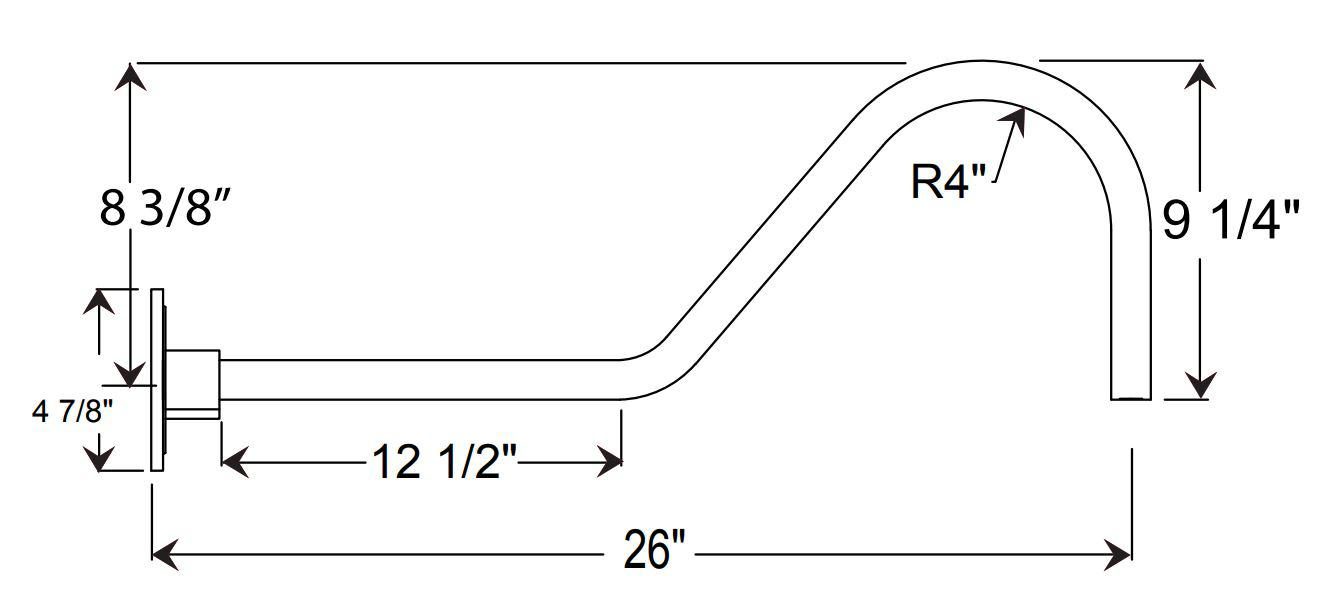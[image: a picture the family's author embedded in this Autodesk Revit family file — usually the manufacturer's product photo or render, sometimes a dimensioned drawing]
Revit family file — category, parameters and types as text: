
# Revit family: OSND MB 24,36,42
name_source: partatom
category: Lighting Fixtures
units: mm (PartAtom-declared; Revit-internal decimal feet)

## family parameters
Always vertical = Yes
Cut with Voids When Loaded = No
Light Source = Yes
OmniClass Number = 23.80.70.00
OmniClass Title = Lighting
Part Type = Normal
Room Calculation Point = No
Round Connector Dimension = Use Diameter
Shared = No
Work Plane-Based = No

## types (3) — shared parameters
Apparent Load = 200 VA
Body Colour = Spun aluminium
Body Material = body
Bulb = Bulb
CRI = >90
Canopy Body = body
Color Filter = 16777215
Construction Material = Heavy Duty spun aluminum.
Default Elevation = 0' - 0"
Description = 120-277 Voltage
Dimming = 1%
Dimming Lamp Color Temperature Shift = <None>
Efficiency = 65-125 lumens per watt
Lamp = MB
Life = L70 50,000 hours
Load Classification = Lighting
Manufacturer = ANP Lighting
Photometric Web File = generic
Power Factor = 1
Tilt Angle = 90.00°
URL = https://www.anplighting.com
Voltage = 277 V
Warranty = 5 year limited warranty
Wattage Comments = 200 W Max

## per-type parameters (varying)
| type | Fixture Diameter | Fixture Height | OSND24 | OSND36 | OSND42 | Weight | a | b |
| OSND24 | 2' - 0" | 1' - 8" | Yes | No | No | 9.0 lbs | 1' - 8" | 0' - 7" |
| OSND36 | 3' - 0" | 2' - 2" | No | Yes | No | 20.0 lbs | 2' - 2" | 0' - 10" |
| OSND42 | 3' - 6" | 2' - 5" | No | No | Yes | 25.5 lbs | 2' - 5" | 0' - 6" |

note: column(s) folded — value = type name in every type: Model

## geometry (parser evidence)
native form markers: Sweep x35
no freeform markers — native parametric forms only
